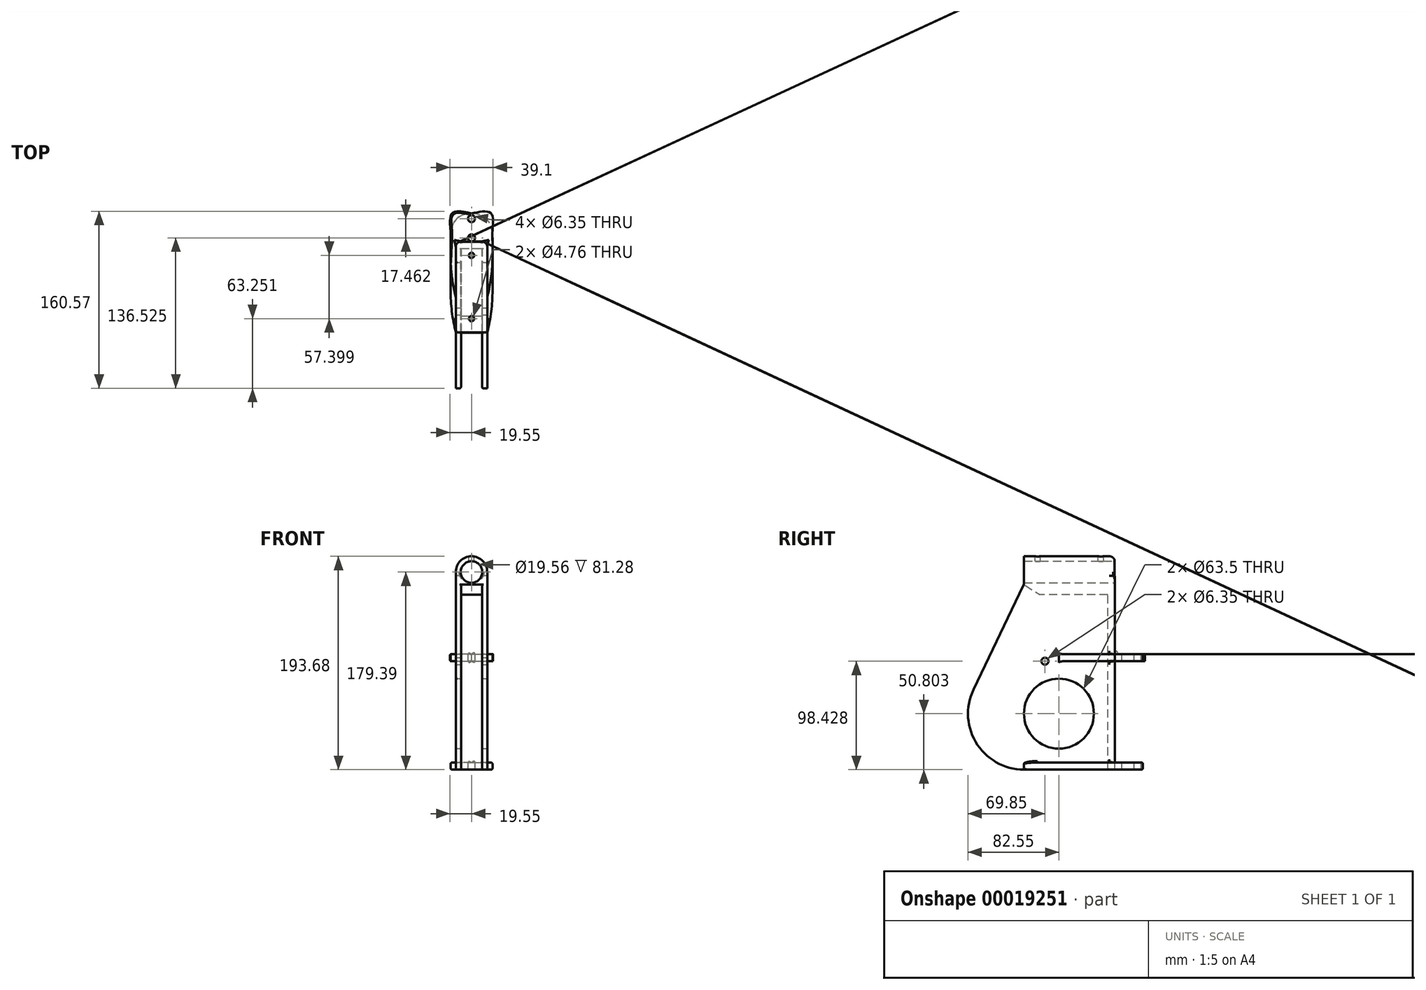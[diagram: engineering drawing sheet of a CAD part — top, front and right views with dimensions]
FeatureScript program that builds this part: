
annotation { "Feature Type Name" : "Feature", "Feature Type Description" : "" }
export const myFeature = defineFeature(function(context is Context, id is Id, definition is map)
    precondition{}
    {
        {
            var Q0;
            Q0=qCreatedBy(makeId("Front.planeOp"),FACE);
            var sketch = newSketch(context, id + "F0", { "sketchPlane" : qUnion([Q0])});
            skLineSegment(sketch, "E0.rect.top", {"start": v(-14.29, -96.84) * mm, "end": v(14.29, -96.84) * mm});
            skLineSegment(sketch, "E0.rect.left", {"start": v(-14.29, 82.55) * mm, "end": v(-14.29, -96.84) * mm});
            skLineSegment(sketch, "E0.rect.right", {"start": v(14.29, 82.55) * mm, "end": v(14.29, -96.84) * mm});
            skPoint(sketch, "E0.rect.middle", {"position": v(0, 0) * mm});
            skCircle(sketch, "E1", {"center": v(0, 82.55) * mm, "radius": 9.78 * mm});
            skArc(sketch, "E2", {"start": v(14.29, 82.55) * mm, "mid": v(0, 96.84) * mm, "end": v(-14.29, 82.55) * mm});
            skPoint(sketch, "E3.orphan", {"position": v(-14.29, 96.84) * mm});
            skPoint(sketch, "E4.orphan", {"position": v(14.29, 96.84) * mm});
            skSolve(sketch);
        }
        {
            var Q0;
            Q0=makeQuery(id+"F0.imprint","IMPRINT",FACE,{"disambiguationData":[TD([[makeQuery(id+"F0.imprint","IMPRINT",EDGE,{"derivedFrom":sQuery(id+"F0.wireOp",EDGE,"E0.rect.top")}),1.0]])]});
            extrude(context, id + "F1", {"entities" : qUnion([Q0]), "depth" : 133.35 * mm});
        }
        {
            var Q0;
            Q0=makeQuery(id+"F1.opExtrude","CAP_FACE",FACE,{"disambiguationData":[OSD([sQuery(id+"F0.wireOp",EDGE,"E0.rect.top"),sQuery(id+"F0.wireOp",EDGE,"E0.rect.left"),sQuery(id+"F0.wireOp",EDGE,"E0.rect.right"),sQuery(id+"F0.wireOp",EDGE,"E1"),sQuery(id+"F0.wireOp",EDGE,"E2")])],"isStart":false});
            var sketch = newSketch(context, id + "F2", { "sketchPlane" : qUnion([Q0])});
            skLineSegment(sketch, "E5.bottom", {"start": v(-9.53, -96.84) * mm, "end": v(9.52, -96.84) * mm});
            skLineSegment(sketch, "E5.top", {"start": v(-9.53, 61.91) * mm, "end": v(9.53, 61.91) * mm});
            skLineSegment(sketch, "E5.left", {"start": v(-9.53, -96.84) * mm, "end": v(-9.53, 61.91) * mm});
            skLineSegment(sketch, "E5.right", {"start": v(9.52, -96.84) * mm, "end": v(9.53, 61.91) * mm});
            skSolve(sketch);
        }
        {
            var Q0;
            Q0=makeQuery(id+"F2.imprint","IMPRINT",FACE,{"disambiguationData":[TD([[makeQuery(id+"F2.imprint","IMPRINT",EDGE,{"derivedFrom":sQuery(id+"F2.wireOp",EDGE,"E5.bottom")}),1.0]])]});
            extrude(context, id + "F3", {"entities" : qUnion([Q0]), "operationType" : NewBodyOperationType.REMOVE, "oppositeDirection" : true, "depth" : 127 * mm});
        }
        {
            var Q0;
            Q0=makeQuery(id+"F1.opExtrude","SWEPT_FACE",FACE,{"disambiguationData":[OSD([sQuery(id+"F0.wireOp",EDGE,"E0.rect.right")])]});
            var sketch = newSketch(context, id + "F4", { "sketchPlane" : qUnion([Q0])});
            skLineSegment(sketch, "E6", {"start": v(-82.55, 96.84) * mm, "end": v(-82.55, 71.44) * mm});
            skLineSegment(sketch, "E7", {"start": v(-82.55, 71.44) * mm, "end": v(-128.35, -24.07) * mm});
            skLineSegment(sketch, "E8", {"start": v(-82.55, -96.84) * mm, "end": v(0, -96.84) * mm});
            skLineSegment(sketch, "E9", {"start": v(0, -96.84) * mm, "end": v(0, 96.84) * mm});
            skLineSegment(sketch, "E10", {"start": v(0, 96.84) * mm, "end": v(-82.55, 96.84) * mm});
            skArc(sketch, "E11", {"start": v(-128.35, -24.07) * mm, "mid": v(-125.54, -73.1) * mm, "end": v(-82.55, -96.84) * mm});
            skLineSegment(sketch, "E12", {"start": v(-133.35, 96.84) * mm, "end": v(0, 96.84) * mm, "construction": true});
            skLineSegment(sketch, "E13", {"start": v(-82.55, 96.84) * mm, "end": v(-104.63, 136.99) * mm});
            skLineSegment(sketch, "E14", {"start": v(-104.63, 136.99) * mm, "end": v(-256.41, 126.94) * mm});
            skLineSegment(sketch, "E15", {"start": v(-256.41, 126.94) * mm, "end": v(-191.56, -96.27) * mm});
            skLineSegment(sketch, "E16", {"start": v(-191.56, -96.27) * mm, "end": v(-69.42, -120.07) * mm});
            skLineSegment(sketch, "E17", {"start": v(-69.42, -120.07) * mm, "end": v(-82.55, -96.84) * mm});
            skSolve(sketch);
        }
        {
            var Q0;
            {var subQ11=sQuery(id+"F4.wireOp",EDGE,"E13");Q0=makeQuery(id+"F4.imprint","IMPRINT",FACE,{"disambiguationData":[TD([[makeQuery(id+"F4.imprint","IMPRINT",EDGE,{"derivedFrom":subQ11}),1.0]])]});}
            var Q1;
            {var subQ8=sQuery(id+"F4.wireOp",EDGE,"E7");Q1=makeQuery(id+"F4.imprint","IMPRINT",FACE,{"disambiguationData":[TD([[makeQuery(id+"F4.imprint","IMPRINT",EDGE,{"derivedFrom":subQ8}),-1.0]])]});}
            var Q2;
            {var subQ0=sQuery(id+"F0.wireOp",EDGE,"E0.rect.right");var subQ1=makeQuery(id+"F1.opExtrude","CAP_EDGE",EDGE,{"disambiguationData":[OSD([subQ0])],"isStart":false});var subQ2=sQuery(id+"F4.wireOp",EDGE,"E11");var subQ3=makeQuery(id+"F4.imprint","INTERSECT",VERTEX,{"derivedFrom":[subQ1,subQ2]});Q2=makeQuery(id+"F4.imprint","IMPRINT",FACE,{"disambiguationData":[TD([[makeQuery(id+"F4.imprint","IMPRINT",EDGE,{"disambiguationData":[TD([[subQ3,-1.0]])],"derivedFrom":subQ1}),1.0]])]});}
            extrude(context, id + "F5", {"entities" : qUnion([Q0, Q1, Q2]), "operationType" : NewBodyOperationType.REMOVE, "endBound" : BoundingType.THROUGH_ALL, "oppositeDirection" : true, "depth" : 25.4 * mm});
        }
        {
            var Q0;
            Q0=makeQuery(id+"F5.boolean.opBoolean","INTERSECT",EDGE,{"derivedFrom":[makeQuery(id+"F3.boolean.opBoolean","COPY",FACE,{"derivedFrom":makeQuery(id+"F3.opExtrude","SWEPT_FACE",FACE,{"disambiguationData":[OSD([sQuery(id+"F2.wireOp",EDGE,"E5.top")])]})}),makeQuery(id+"F5.opExtrude","SWEPT_FACE",FACE,{"disambiguationData":[OSD([sQuery(id+"F4.wireOp",EDGE,"E7")])]})]});
            chamfer(context, id + "F6", {"entities" : qUnion([Q0]), "chamferType" : ChamferType.TWO_OFFSETS, "width1" : 19.05 * mm, "oppositeDirection" : false, "width2" : 10.16 * mm, "tangentPropagation" : true});
        }
        {
            var Q0;
            Q0=makeQuery(id+"F5.boolean.opBoolean","COPY",EDGE,{"derivedFrom":makeQuery(id+"F5.opExtrude","SWEPT_EDGE",EDGE,{"disambiguationData":[OSD([sQuery(id+"F4.wireOp",EDGE,"E6"),sQuery(id+"F4.wireOp",EDGE,"E7")])]})});
            fillet(context, id + "F7", {"entities" : qUnion([Q0]), "radius" : 6.35 * mm, "tangentPropagation" : true, "allowEdgeOverflow" : false});
        }
        {
            var Q0;
            Q0=makeQuery(id+"F1.opExtrude","SWEPT_FACE",FACE,{"disambiguationData":[OSD([sQuery(id+"F0.wireOp",EDGE,"E0.rect.right")])]});
            var sketch = newSketch(context, id + "F8", { "sketchPlane" : qUnion([Q0])});
            skCircle(sketch, "E18", {"center": v(-50.8, -46.04) * mm, "radius": 31.75 * mm});
            skSolve(sketch);
        }
        {
            var Q0;
            Q0=makeQuery(id+"F8.imprint","IMPRINT",FACE,{"disambiguationData":[TD([[makeQuery(id+"F8.imprint","IMPRINT",EDGE,{"derivedFrom":sQuery(id+"F8.wireOp",EDGE,"E18")}),1.0]])]});
            extrude(context, id + "F9", {"entities" : qUnion([Q0]), "operationType" : NewBodyOperationType.REMOVE, "endBound" : BoundingType.THROUGH_ALL, "oppositeDirection" : true, "depth" : 25.4 * mm});
        }
        {
            var Q0;
            Q0=makeQuery(id+"F1.opExtrude","SWEPT_FACE",FACE,{"disambiguationData":[OSD([sQuery(id+"F0.wireOp",EDGE,"E0.rect.top")])]});
            var sketch = newSketch(context, id + "F10", { "sketchPlane" : qUnion([Q0])});
            skLineSegment(sketch, "E19", {"start": v(0, -25.4) * mm, "end": v(0, 82.55) * mm, "construction": true});
            skLineSegment(sketch, "E20", {"start": v(-19.05, 44.45) * mm, "end": v(-19.05, 0) * mm});
            skArc(sketch, "E21", {"start": v(-14.29, 82.55) * mm, "mid": v(-17.85, 63.65) * mm, "end": v(-19.05, 44.45) * mm});
            skFitSpline(sketch, "E22", {"points": [v(0, -25.4) * mm, v(-19.05, 0) * mm], "startDerivative": vector(-53.17, 0) * mm, "endDerivative": vector(0, 31.35) * mm});
            skArc(sketch, "E23.MirrorCS", {"start": v(14.29, 82.55) * mm, "mid": v(17.85, 63.65) * mm, "end": v(19.05, 44.45) * mm});
            skLineSegment(sketch, "E24.MirrorCS", {"start": v(19.05, 44.45) * mm, "end": v(19.05, 0) * mm});
            skFitSpline(sketch, "E25.MirrorCS", {"points": [v(0, -25.4) * mm, v(19.05, 0) * mm], "startDerivative": vector(53.17, 0) * mm, "endDerivative": vector(0, 31.35) * mm});
            skLineSegment(sketch, "E26", {"start": v(-14.29, 82.55) * mm, "end": v(-9.53, 82.55) * mm});
            skLineSegment(sketch, "E27", {"start": v(-9.53, 82.55) * mm, "end": v(-9.53, 6.35) * mm});
            skLineSegment(sketch, "E28", {"start": v(-9.53, 6.35) * mm, "end": v(9.52, 6.35) * mm});
            skLineSegment(sketch, "E29", {"start": v(9.52, 6.35) * mm, "end": v(9.53, 82.55) * mm});
            skLineSegment(sketch, "E30", {"start": v(9.53, 82.55) * mm, "end": v(14.29, 82.55) * mm});
            skSolve(sketch);
        }
        {
            var Q0;
            Q0 = qSketchRegion(id + "F10", true);
            extrude(context, id + "F11", {"entities" : qUnion([Q0]), "operationType" : NewBodyOperationType.ADD, "oppositeDirection" : true, "depth" : 6.35 * mm});
        }
        {
            var Q0;
            Q0=makeQuery(id+"F11.boolean.opBoolean","MERGE",FACE,{"derivedFrom":[makeQuery(id+"F1.opExtrude","SWEPT_FACE",FACE,{"disambiguationData":[OSD([sQuery(id+"F0.wireOp",EDGE,"E0.rect.top")])]}),makeQuery(id+"F11.opExtrude","CAP_FACE",FACE,{"disambiguationData":[OSD([sQuery(id+"F10.wireOp",EDGE,"E20"),sQuery(id+"F10.wireOp",EDGE,"E21"),sQuery(id+"F10.wireOp",EDGE,"E22"),sQuery(id+"F10.wireOp",EDGE,"E23.MirrorCS"),sQuery(id+"F10.wireOp",EDGE,"E24.MirrorCS"),sQuery(id+"F10.wireOp",EDGE,"E25.MirrorCS"),sQuery(id+"F10.wireOp",EDGE,"E26"),sQuery(id+"F10.wireOp",EDGE,"E27"),sQuery(id+"F10.wireOp",EDGE,"E28"),sQuery(id+"F10.wireOp",EDGE,"E29"),sQuery(id+"F10.wireOp",EDGE,"E30")])],"isStart":true})]});
            cPlane(context, id + "F12", {"entities" : qUnion([Q0]), "cplaneType" : CPlaneType.OFFSET, "offset" : 101.6 * mm, "oppositeDirection" : true, "width" : 152.4 * mm, "height" : 152.4 * mm});
        }
        {
            var Q0;
            Q0=qCreatedBy(id+"F12.planeOp",FACE);
            var sketch = newSketch(context, id + "F13", { "sketchPlane" : qUnion([Q0])});
            skLineSegment(sketch, "E31.0", {"start": v(0, -25.4) * mm, "end": v(0, 82.55) * mm, "construction": true});
            skLineSegment(sketch, "E31.1", {"start": v(-19.05, 12.7) * mm, "end": v(-19.05, 0) * mm});
            skArc(sketch, "E31.2", {"start": v(-14.29, 50.8) * mm, "mid": v(-17.85, 31.9) * mm, "end": v(-19.05, 12.7) * mm});
            skFitSpline(sketch, "E31.3", {"points": [v(0, -25.4) * mm, v(-17.72, -25.4) * mm, v(-19.05, -10.45) * mm, v(-19.05, 0) * mm]});
            skArc(sketch, "E31.4", {"start": v(14.29, 50.8) * mm, "mid": v(17.85, 31.9) * mm, "end": v(19.05, 12.7) * mm});
            skLineSegment(sketch, "E31.5", {"start": v(19.05, 12.7) * mm, "end": v(19.05, 0) * mm});
            skFitSpline(sketch, "E31.6", {"points": [v(0, -25.4) * mm, v(17.72, -25.4) * mm, v(19.05, -10.45) * mm, v(19.05, 0) * mm]});
            skLineSegment(sketch, "E31.8", {"start": v(-9.53, 50.8) * mm, "end": v(-9.53, 6.35) * mm});
            skLineSegment(sketch, "E31.9", {"start": v(-9.53, 6.35) * mm, "end": v(9.52, 6.35) * mm});
            skLineSegment(sketch, "E31.10", {"start": v(9.53, 6.35) * mm, "end": v(9.53, 50.8) * mm});
            skLineSegment(sketch, "E32", {"start": v(-9.53, 50.8) * mm, "end": v(-14.29, 50.8) * mm});
            skLineSegment(sketch, "E33", {"start": v(9.53, 50.8) * mm, "end": v(14.29, 50.8) * mm});
            skSolve(sketch);
        }
        {
            var Q0;
            Q0=makeQuery(id+"F13.imprint","IMPRINT",FACE,{"disambiguationData":[TD([[makeQuery(id+"F13.imprint","IMPRINT",EDGE,{"derivedFrom":sQuery(id+"F13.wireOp",EDGE,"E31.1")}),1.0]])]});
            extrude(context, id + "F14", {"entities" : qUnion([Q0]), "operationType" : NewBodyOperationType.ADD, "endBound" : BoundingType.SYMMETRIC, "depth" : 6.35 * mm});
        }
        {
            var Q0;
            Q0=makeQuery(id+"F1.opExtrude","SWEPT_FACE",FACE,{"disambiguationData":[OSD([sQuery(id+"F0.wireOp",EDGE,"E0.rect.right")])]});
            var sketch = newSketch(context, id + "F15", { "sketchPlane" : qUnion([Q0])});
            skCircle(sketch, "E34", {"center": v(-63.5, 1.59) * mm, "radius": 3.18 * mm});
            skSolve(sketch);
        }
        {
            var Q0;
            Q0=makeQuery(id+"F15.imprint","IMPRINT",FACE,{"disambiguationData":[TD([[makeQuery(id+"F15.imprint","IMPRINT",EDGE,{"derivedFrom":sQuery(id+"F15.wireOp",EDGE,"E34")}),1.0]])]});
            extrude(context, id + "F16", {"entities" : qUnion([Q0]), "operationType" : NewBodyOperationType.REMOVE, "endBound" : BoundingType.THROUGH_ALL, "oppositeDirection" : true, "depth" : 25.4 * mm});
        }
        {
            var Q0;
            Q0=makeQuery(id+"F14.opExtrude","CAP_FACE",FACE,{"disambiguationData":[OSD([sQuery(id+"F13.wireOp",EDGE,"E31.1"),sQuery(id+"F13.wireOp",EDGE,"E31.2"),sQuery(id+"F13.wireOp",EDGE,"E31.3"),sQuery(id+"F13.wireOp",EDGE,"E31.4"),sQuery(id+"F13.wireOp",EDGE,"E31.5"),sQuery(id+"F13.wireOp",EDGE,"E31.6"),sQuery(id+"F13.wireOp",EDGE,"E31.8"),sQuery(id+"F13.wireOp",EDGE,"E31.9"),sQuery(id+"F13.wireOp",EDGE,"E31.10"),sQuery(id+"F13.wireOp",EDGE,"E32"),sQuery(id+"F13.wireOp",EDGE,"E33")])],"isStart":true});
            var sketch = newSketch(context, id + "F17", { "sketchPlane" : qUnion([Q0])});
            skCircle(sketch, "E35", {"center": v(0, 3.18) * mm, "radius": 3.18 * mm});
            skSolve(sketch);
        }
        {
            var Q0;
            Q0=makeQuery(id+"F17.imprint","IMPRINT",FACE,{"disambiguationData":[TD([[makeQuery(id+"F17.imprint","IMPRINT",EDGE,{"derivedFrom":sQuery(id+"F17.wireOp",EDGE,"E35")}),1.0]])]});
            extrude(context, id + "F18", {"entities" : qUnion([Q0]), "operationType" : NewBodyOperationType.REMOVE, "endBound" : BoundingType.THROUGH_ALL, "oppositeDirection" : true, "depth" : 25.4 * mm});
        }
        {
            var Q0;
            Q0=makeQuery(id+"F14.opExtrude","CAP_FACE",FACE,{"disambiguationData":[OSD([sQuery(id+"F13.wireOp",EDGE,"E31.1"),sQuery(id+"F13.wireOp",EDGE,"E31.2"),sQuery(id+"F13.wireOp",EDGE,"E31.3"),sQuery(id+"F13.wireOp",EDGE,"E31.4"),sQuery(id+"F13.wireOp",EDGE,"E31.5"),sQuery(id+"F13.wireOp",EDGE,"E31.6"),sQuery(id+"F13.wireOp",EDGE,"E31.8"),sQuery(id+"F13.wireOp",EDGE,"E31.9"),sQuery(id+"F13.wireOp",EDGE,"E31.10"),sQuery(id+"F13.wireOp",EDGE,"E32"),sQuery(id+"F13.wireOp",EDGE,"E33")])],"isStart":true});
            var sketch = newSketch(context, id + "F19", { "sketchPlane" : qUnion([Q0])});
            skCircle(sketch, "E36", {"center": v(0, 20.64) * mm, "radius": 3.18 * mm});
            skSolve(sketch);
        }
        {
            var Q0;
            Q0 = qSketchRegion(id + "F19", true);
            extrude(context, id + "F20", {"entities" : qUnion([Q0]), "operationType" : NewBodyOperationType.REMOVE, "endBound" : BoundingType.THROUGH_ALL, "oppositeDirection" : true, "depth" : 25.4 * mm});
        }
        {
            var Q0;
            {var subQ0=sQuery(id+"F0.wireOp",EDGE,"E0.rect.left");var subQ1=sQuery(id+"F0.wireOp",EDGE,"E0.rect.right");var subQ2=sQuery(id+"F0.wireOp",EDGE,"E1");var subQ3=sQuery(id+"F0.wireOp",EDGE,"E2");Q0=makeQuery(id+"F14.boolean.opBoolean","SPLIT",FACE,{"disambiguationData":[TD([makeQuery(id+"F1.opExtrude","SWEPT_FACE",FACE,{"disambiguationData":[OSD([subQ2])]})])],"derivedFrom":makeQuery(id+"F1.opExtrude","CAP_FACE",FACE,{"disambiguationData":[OSD([sQuery(id+"F0.wireOp",EDGE,"E0.rect.top"),subQ0,subQ1,subQ2,subQ3])],"isStart":true})});}
            var sketch = newSketch(context, id + "F21", { "sketchPlane" : qUnion([Q0])});
            skArc(sketch, "E37.0", {"start": v(-14.29, 82.55) * mm, "mid": v(0, 96.84) * mm, "end": v(14.29, 82.55) * mm});
            skPoint(sketch, "E38", {"position": v(0, 96.84) * mm});
            skSolve(sketch);
        }
        {
            var Q0;
            Q0=sQuery(id+"F21.wireOp",VERTEX,"E38");
            var Q1;
            Q1=makeQuery(id+"F14.opExtrude","CAP_FACE",FACE,{"disambiguationData":[OSD([sQuery(id+"F13.wireOp",EDGE,"E31.1"),sQuery(id+"F13.wireOp",EDGE,"E31.2"),sQuery(id+"F13.wireOp",EDGE,"E31.3"),sQuery(id+"F13.wireOp",EDGE,"E31.4"),sQuery(id+"F13.wireOp",EDGE,"E31.5"),sQuery(id+"F13.wireOp",EDGE,"E31.6"),sQuery(id+"F13.wireOp",EDGE,"E31.8"),sQuery(id+"F13.wireOp",EDGE,"E31.9"),sQuery(id+"F13.wireOp",EDGE,"E31.10"),sQuery(id+"F13.wireOp",EDGE,"E32"),sQuery(id+"F13.wireOp",EDGE,"E33")])],"isStart":true});
            cPlane(context, id + "F22", {"entities" : qUnion([Q0, Q1]), "cplaneType" : CPlaneType.PLANE_POINT, "offset" : 152.4 * mm, "width" : 152.4 * mm, "height" : 152.4 * mm});
        }
        {
            var Q0;
            Q0=qCreatedBy(id+"F22.planeOp",FACE);
            var sketch = newSketch(context, id + "F23", { "sketchPlane" : qUnion([Q0])});
            skLineSegment(sketch, "E39", {"start": v(0, 0) * mm, "end": v(0, -82.55) * mm, "construction": true});
            skCircle(sketch, "E40", {"center": v(0, -12.7) * mm, "radius": 2.38 * mm});
            skCircle(sketch, "E41", {"center": v(0, -70.1) * mm, "radius": 2.38 * mm});
            skSolve(sketch);
        }
        {
            var Q0;
            Q0=makeQuery(id+"F23.imprint","IMPRINT",FACE,{"disambiguationData":[TD([[makeQuery(id+"F23.imprint","IMPRINT",EDGE,{"derivedFrom":sQuery(id+"F23.wireOp",EDGE,"E40")}),1.0]])]});
            var Q1;
            Q1=makeQuery(id+"F23.imprint","IMPRINT",FACE,{"disambiguationData":[TD([[makeQuery(id+"F23.imprint","IMPRINT",EDGE,{"derivedFrom":sQuery(id+"F23.wireOp",EDGE,"E41")}),1.0]])]});
            extrude(context, id + "F24", {"entities" : qUnion([Q0, Q1]), "operationType" : NewBodyOperationType.REMOVE, "oppositeDirection" : true, "depth" : 6.35 * mm});
        }
        {
            var Q0;
            Q0=makeQuery(id+"F9.boolean.opBoolean","COPY",EDGE,{"derivedFrom":makeQuery(id+"F9.opExtrude","CAP_EDGE",EDGE,{"disambiguationData":[OSD([sQuery(id+"F8.wireOp",EDGE,"E18")])],"isStart":true})});
            var Q1;
            Q1=makeQuery(id+"F9.boolean.opBoolean","INTERSECT",EDGE,{"derivedFrom":[makeQuery(id+"F3.boolean.opBoolean","COPY",FACE,{"derivedFrom":makeQuery(id+"F3.opExtrude","SWEPT_FACE",FACE,{"disambiguationData":[OSD([sQuery(id+"F2.wireOp",EDGE,"E5.right")])]})}),makeQuery(id+"F9.opExtrude","SWEPT_FACE",FACE,{"disambiguationData":[OSD([sQuery(id+"F8.wireOp",EDGE,"E18")])]})]});
            var Q2;
            Q2=makeQuery(id+"F9.boolean.opBoolean","INTERSECT",EDGE,{"derivedFrom":[makeQuery(id+"F3.boolean.opBoolean","COPY",FACE,{"derivedFrom":makeQuery(id+"F3.opExtrude","SWEPT_FACE",FACE,{"disambiguationData":[OSD([sQuery(id+"F2.wireOp",EDGE,"E5.left")])]})}),makeQuery(id+"F9.opExtrude","SWEPT_FACE",FACE,{"disambiguationData":[OSD([sQuery(id+"F8.wireOp",EDGE,"E18")])]})]});
            var Q3;
            Q3=makeQuery(id+"F9.boolean.opBoolean","INTERSECT",EDGE,{"derivedFrom":[makeQuery(id+"F1.opExtrude","SWEPT_FACE",FACE,{"disambiguationData":[OSD([sQuery(id+"F0.wireOp",EDGE,"E0.rect.left")])]}),makeQuery(id+"F9.opExtrude","SWEPT_FACE",FACE,{"disambiguationData":[OSD([sQuery(id+"F8.wireOp",EDGE,"E18")])]})]});
            var Q4;
            Q4=makeQuery(id+"F5.boolean.opBoolean","COPY",EDGE,{"derivedFrom":makeQuery(id+"F5.opExtrude","CAP_EDGE",EDGE,{"disambiguationData":[OSD([sQuery(id+"F4.wireOp",EDGE,"E7")])],"isStart":true})});
            var Q5;
            Q5=makeQuery(id+"F14.boolean.opBoolean","INTERSECT",EDGE,{"derivedFrom":[makeQuery(id+"F1.opExtrude","SWEPT_FACE",FACE,{"disambiguationData":[OSD([sQuery(id+"F0.wireOp",EDGE,"E0.rect.right")])]}),makeQuery(id+"F14.opExtrude","CAP_FACE",FACE,{"disambiguationData":[OSD([sQuery(id+"F13.wireOp",EDGE,"E31.1"),sQuery(id+"F13.wireOp",EDGE,"E31.2"),sQuery(id+"F13.wireOp",EDGE,"E31.3"),sQuery(id+"F13.wireOp",EDGE,"E31.4"),sQuery(id+"F13.wireOp",EDGE,"E31.5"),sQuery(id+"F13.wireOp",EDGE,"E31.6"),sQuery(id+"F13.wireOp",EDGE,"E31.8"),sQuery(id+"F13.wireOp",EDGE,"E31.9"),sQuery(id+"F13.wireOp",EDGE,"E31.10"),sQuery(id+"F13.wireOp",EDGE,"E32"),sQuery(id+"F13.wireOp",EDGE,"E33")])],"isStart":true})]});
            var Q6;
            {var subQ0=sQuery(id+"F0.wireOp",EDGE,"E0.rect.right");var subQ1=makeQuery(id+"F1.opExtrude","CAP_FACE",FACE,{"disambiguationData":[OSD([sQuery(id+"F0.wireOp",EDGE,"E0.rect.top"),sQuery(id+"F0.wireOp",EDGE,"E0.rect.left"),subQ0,sQuery(id+"F0.wireOp",EDGE,"E1"),sQuery(id+"F0.wireOp",EDGE,"E2")])],"isStart":true});var subQ2=makeQuery(id+"F14.opExtrude","CAP_FACE",FACE,{"disambiguationData":[OSD([sQuery(id+"F13.wireOp",EDGE,"E31.1"),sQuery(id+"F13.wireOp",EDGE,"E31.2"),sQuery(id+"F13.wireOp",EDGE,"E31.3"),sQuery(id+"F13.wireOp",EDGE,"E31.4"),sQuery(id+"F13.wireOp",EDGE,"E31.5"),sQuery(id+"F13.wireOp",EDGE,"E31.6"),sQuery(id+"F13.wireOp",EDGE,"E31.8"),sQuery(id+"F13.wireOp",EDGE,"E31.9"),sQuery(id+"F13.wireOp",EDGE,"E31.10"),sQuery(id+"F13.wireOp",EDGE,"E32"),sQuery(id+"F13.wireOp",EDGE,"E33")])],"isStart":true});Q6=makeQuery(id+"F18.boolean.opBoolean","SPLIT",EDGE,{"disambiguationData":[TD([makeQuery(id+"F1.opExtrude","SWEPT_FACE",FACE,{"disambiguationData":[OSD([subQ0])]})])],"derivedFrom":makeQuery(id+"F14.boolean.opBoolean","INTERSECT",EDGE,{"derivedFrom":[subQ1,subQ2]})});}
            var Q7;
            {var subQ0=sQuery(id+"F0.wireOp",EDGE,"E0.rect.left");var subQ1=makeQuery(id+"F1.opExtrude","CAP_FACE",FACE,{"disambiguationData":[OSD([sQuery(id+"F0.wireOp",EDGE,"E0.rect.top"),subQ0,sQuery(id+"F0.wireOp",EDGE,"E0.rect.right"),sQuery(id+"F0.wireOp",EDGE,"E1"),sQuery(id+"F0.wireOp",EDGE,"E2")])],"isStart":true});var subQ2=makeQuery(id+"F14.opExtrude","CAP_FACE",FACE,{"disambiguationData":[OSD([sQuery(id+"F13.wireOp",EDGE,"E31.1"),sQuery(id+"F13.wireOp",EDGE,"E31.2"),sQuery(id+"F13.wireOp",EDGE,"E31.3"),sQuery(id+"F13.wireOp",EDGE,"E31.4"),sQuery(id+"F13.wireOp",EDGE,"E31.5"),sQuery(id+"F13.wireOp",EDGE,"E31.6"),sQuery(id+"F13.wireOp",EDGE,"E31.8"),sQuery(id+"F13.wireOp",EDGE,"E31.9"),sQuery(id+"F13.wireOp",EDGE,"E31.10"),sQuery(id+"F13.wireOp",EDGE,"E32"),sQuery(id+"F13.wireOp",EDGE,"E33")])],"isStart":true});Q7=makeQuery(id+"F18.boolean.opBoolean","SPLIT",EDGE,{"disambiguationData":[TD([makeQuery(id+"F1.opExtrude","SWEPT_FACE",FACE,{"disambiguationData":[OSD([subQ0])]})])],"derivedFrom":makeQuery(id+"F14.boolean.opBoolean","INTERSECT",EDGE,{"derivedFrom":[subQ1,subQ2]})});}
            var Q8;
            Q8=makeQuery(id+"F14.boolean.opBoolean","INTERSECT",EDGE,{"derivedFrom":[makeQuery(id+"F1.opExtrude","SWEPT_FACE",FACE,{"disambiguationData":[OSD([sQuery(id+"F0.wireOp",EDGE,"E0.rect.left")])]}),makeQuery(id+"F14.opExtrude","CAP_FACE",FACE,{"disambiguationData":[OSD([sQuery(id+"F13.wireOp",EDGE,"E31.1"),sQuery(id+"F13.wireOp",EDGE,"E31.2"),sQuery(id+"F13.wireOp",EDGE,"E31.3"),sQuery(id+"F13.wireOp",EDGE,"E31.4"),sQuery(id+"F13.wireOp",EDGE,"E31.5"),sQuery(id+"F13.wireOp",EDGE,"E31.6"),sQuery(id+"F13.wireOp",EDGE,"E31.8"),sQuery(id+"F13.wireOp",EDGE,"E31.9"),sQuery(id+"F13.wireOp",EDGE,"E31.10"),sQuery(id+"F13.wireOp",EDGE,"E32"),sQuery(id+"F13.wireOp",EDGE,"E33")])],"isStart":true})]});
            var Q9;
            Q9=makeQuery(id+"F14.boolean.opBoolean","INTERSECT",EDGE,{"derivedFrom":[makeQuery(id+"F1.opExtrude","SWEPT_FACE",FACE,{"disambiguationData":[OSD([sQuery(id+"F0.wireOp",EDGE,"E0.rect.left")])]}),makeQuery(id+"F14.opExtrude","CAP_FACE",FACE,{"disambiguationData":[OSD([sQuery(id+"F13.wireOp",EDGE,"E31.1"),sQuery(id+"F13.wireOp",EDGE,"E31.2"),sQuery(id+"F13.wireOp",EDGE,"E31.3"),sQuery(id+"F13.wireOp",EDGE,"E31.4"),sQuery(id+"F13.wireOp",EDGE,"E31.5"),sQuery(id+"F13.wireOp",EDGE,"E31.6"),sQuery(id+"F13.wireOp",EDGE,"E31.8"),sQuery(id+"F13.wireOp",EDGE,"E31.9"),sQuery(id+"F13.wireOp",EDGE,"E31.10"),sQuery(id+"F13.wireOp",EDGE,"E32"),sQuery(id+"F13.wireOp",EDGE,"E33")])],"isStart":false})]});
            var Q10;
            {var subQ0=sQuery(id+"F0.wireOp",EDGE,"E0.rect.left");var subQ1=makeQuery(id+"F1.opExtrude","CAP_FACE",FACE,{"disambiguationData":[OSD([sQuery(id+"F0.wireOp",EDGE,"E0.rect.top"),subQ0,sQuery(id+"F0.wireOp",EDGE,"E0.rect.right"),sQuery(id+"F0.wireOp",EDGE,"E1"),sQuery(id+"F0.wireOp",EDGE,"E2")])],"isStart":true});var subQ2=makeQuery(id+"F14.opExtrude","CAP_FACE",FACE,{"disambiguationData":[OSD([sQuery(id+"F13.wireOp",EDGE,"E31.1"),sQuery(id+"F13.wireOp",EDGE,"E31.2"),sQuery(id+"F13.wireOp",EDGE,"E31.3"),sQuery(id+"F13.wireOp",EDGE,"E31.4"),sQuery(id+"F13.wireOp",EDGE,"E31.5"),sQuery(id+"F13.wireOp",EDGE,"E31.6"),sQuery(id+"F13.wireOp",EDGE,"E31.8"),sQuery(id+"F13.wireOp",EDGE,"E31.9"),sQuery(id+"F13.wireOp",EDGE,"E31.10"),sQuery(id+"F13.wireOp",EDGE,"E32"),sQuery(id+"F13.wireOp",EDGE,"E33")])],"isStart":false});Q10=makeQuery(id+"F18.boolean.opBoolean","SPLIT",EDGE,{"disambiguationData":[TD([makeQuery(id+"F1.opExtrude","SWEPT_FACE",FACE,{"disambiguationData":[OSD([subQ0])]})])],"derivedFrom":makeQuery(id+"F14.boolean.opBoolean","INTERSECT",EDGE,{"derivedFrom":[subQ1,subQ2]})});}
            var Q11;
            {var subQ0=sQuery(id+"F0.wireOp",EDGE,"E0.rect.right");var subQ1=makeQuery(id+"F1.opExtrude","CAP_FACE",FACE,{"disambiguationData":[OSD([sQuery(id+"F0.wireOp",EDGE,"E0.rect.top"),sQuery(id+"F0.wireOp",EDGE,"E0.rect.left"),subQ0,sQuery(id+"F0.wireOp",EDGE,"E1"),sQuery(id+"F0.wireOp",EDGE,"E2")])],"isStart":true});var subQ2=makeQuery(id+"F14.opExtrude","CAP_FACE",FACE,{"disambiguationData":[OSD([sQuery(id+"F13.wireOp",EDGE,"E31.1"),sQuery(id+"F13.wireOp",EDGE,"E31.2"),sQuery(id+"F13.wireOp",EDGE,"E31.3"),sQuery(id+"F13.wireOp",EDGE,"E31.4"),sQuery(id+"F13.wireOp",EDGE,"E31.5"),sQuery(id+"F13.wireOp",EDGE,"E31.6"),sQuery(id+"F13.wireOp",EDGE,"E31.8"),sQuery(id+"F13.wireOp",EDGE,"E31.9"),sQuery(id+"F13.wireOp",EDGE,"E31.10"),sQuery(id+"F13.wireOp",EDGE,"E32"),sQuery(id+"F13.wireOp",EDGE,"E33")])],"isStart":false});Q11=makeQuery(id+"F18.boolean.opBoolean","SPLIT",EDGE,{"disambiguationData":[TD([makeQuery(id+"F1.opExtrude","SWEPT_FACE",FACE,{"disambiguationData":[OSD([subQ0])]})])],"derivedFrom":makeQuery(id+"F14.boolean.opBoolean","INTERSECT",EDGE,{"derivedFrom":[subQ1,subQ2]})});}
            var Q12;
            Q12=makeQuery(id+"F14.boolean.opBoolean","INTERSECT",EDGE,{"derivedFrom":[makeQuery(id+"F1.opExtrude","SWEPT_FACE",FACE,{"disambiguationData":[OSD([sQuery(id+"F0.wireOp",EDGE,"E0.rect.right")])]}),makeQuery(id+"F14.opExtrude","CAP_FACE",FACE,{"disambiguationData":[OSD([sQuery(id+"F13.wireOp",EDGE,"E31.1"),sQuery(id+"F13.wireOp",EDGE,"E31.2"),sQuery(id+"F13.wireOp",EDGE,"E31.3"),sQuery(id+"F13.wireOp",EDGE,"E31.4"),sQuery(id+"F13.wireOp",EDGE,"E31.5"),sQuery(id+"F13.wireOp",EDGE,"E31.6"),sQuery(id+"F13.wireOp",EDGE,"E31.8"),sQuery(id+"F13.wireOp",EDGE,"E31.9"),sQuery(id+"F13.wireOp",EDGE,"E31.10"),sQuery(id+"F13.wireOp",EDGE,"E32"),sQuery(id+"F13.wireOp",EDGE,"E33")])],"isStart":false})]});
            var Q13;
            Q13=makeQuery(id+"F11.boolean.opBoolean","INTERSECT",EDGE,{"derivedFrom":[makeQuery(id+"F1.opExtrude","SWEPT_FACE",FACE,{"disambiguationData":[OSD([sQuery(id+"F0.wireOp",EDGE,"E0.rect.right")])]}),makeQuery(id+"F11.opExtrude","CAP_FACE",FACE,{"disambiguationData":[OSD([sQuery(id+"F10.wireOp",EDGE,"E20"),sQuery(id+"F10.wireOp",EDGE,"E21"),sQuery(id+"F10.wireOp",EDGE,"E22"),sQuery(id+"F10.wireOp",EDGE,"E23.MirrorCS"),sQuery(id+"F10.wireOp",EDGE,"E24.MirrorCS"),sQuery(id+"F10.wireOp",EDGE,"E25.MirrorCS"),sQuery(id+"F10.wireOp",EDGE,"E26"),sQuery(id+"F10.wireOp",EDGE,"E27"),sQuery(id+"F10.wireOp",EDGE,"E28"),sQuery(id+"F10.wireOp",EDGE,"E29"),sQuery(id+"F10.wireOp",EDGE,"E30")])],"isStart":false})]});
            var Q14;
            {var subQ0=sQuery(id+"F0.wireOp",EDGE,"E0.rect.right");var subQ1=makeQuery(id+"F1.opExtrude","CAP_FACE",FACE,{"disambiguationData":[OSD([sQuery(id+"F0.wireOp",EDGE,"E0.rect.top"),sQuery(id+"F0.wireOp",EDGE,"E0.rect.left"),subQ0,sQuery(id+"F0.wireOp",EDGE,"E1"),sQuery(id+"F0.wireOp",EDGE,"E2")])],"isStart":true});var subQ2=makeQuery(id+"F11.opExtrude","CAP_FACE",FACE,{"disambiguationData":[OSD([sQuery(id+"F10.wireOp",EDGE,"E20"),sQuery(id+"F10.wireOp",EDGE,"E21"),sQuery(id+"F10.wireOp",EDGE,"E22"),sQuery(id+"F10.wireOp",EDGE,"E23.MirrorCS"),sQuery(id+"F10.wireOp",EDGE,"E24.MirrorCS"),sQuery(id+"F10.wireOp",EDGE,"E25.MirrorCS"),sQuery(id+"F10.wireOp",EDGE,"E26"),sQuery(id+"F10.wireOp",EDGE,"E27"),sQuery(id+"F10.wireOp",EDGE,"E28"),sQuery(id+"F10.wireOp",EDGE,"E29"),sQuery(id+"F10.wireOp",EDGE,"E30")])],"isStart":false});Q14=makeQuery(id+"F18.boolean.opBoolean","SPLIT",EDGE,{"disambiguationData":[TD([makeQuery(id+"F1.opExtrude","SWEPT_FACE",FACE,{"disambiguationData":[OSD([subQ0])]})])],"derivedFrom":makeQuery(id+"F11.boolean.opBoolean","INTERSECT",EDGE,{"derivedFrom":[subQ1,subQ2]})});}
            var Q15;
            {var subQ0=sQuery(id+"F0.wireOp",EDGE,"E0.rect.left");var subQ1=makeQuery(id+"F1.opExtrude","CAP_FACE",FACE,{"disambiguationData":[OSD([sQuery(id+"F0.wireOp",EDGE,"E0.rect.top"),subQ0,sQuery(id+"F0.wireOp",EDGE,"E0.rect.right"),sQuery(id+"F0.wireOp",EDGE,"E1"),sQuery(id+"F0.wireOp",EDGE,"E2")])],"isStart":true});var subQ2=makeQuery(id+"F11.opExtrude","CAP_FACE",FACE,{"disambiguationData":[OSD([sQuery(id+"F10.wireOp",EDGE,"E20"),sQuery(id+"F10.wireOp",EDGE,"E21"),sQuery(id+"F10.wireOp",EDGE,"E22"),sQuery(id+"F10.wireOp",EDGE,"E23.MirrorCS"),sQuery(id+"F10.wireOp",EDGE,"E24.MirrorCS"),sQuery(id+"F10.wireOp",EDGE,"E25.MirrorCS"),sQuery(id+"F10.wireOp",EDGE,"E26"),sQuery(id+"F10.wireOp",EDGE,"E27"),sQuery(id+"F10.wireOp",EDGE,"E28"),sQuery(id+"F10.wireOp",EDGE,"E29"),sQuery(id+"F10.wireOp",EDGE,"E30")])],"isStart":false});Q15=makeQuery(id+"F18.boolean.opBoolean","SPLIT",EDGE,{"disambiguationData":[TD([makeQuery(id+"F1.opExtrude","SWEPT_FACE",FACE,{"disambiguationData":[OSD([subQ0])]})])],"derivedFrom":makeQuery(id+"F11.boolean.opBoolean","INTERSECT",EDGE,{"derivedFrom":[subQ1,subQ2]})});}
            var Q16;
            Q16=makeQuery(id+"F11.boolean.opBoolean","INTERSECT",EDGE,{"derivedFrom":[makeQuery(id+"F1.opExtrude","SWEPT_FACE",FACE,{"disambiguationData":[OSD([sQuery(id+"F0.wireOp",EDGE,"E0.rect.left")])]}),makeQuery(id+"F11.opExtrude","CAP_FACE",FACE,{"disambiguationData":[OSD([sQuery(id+"F10.wireOp",EDGE,"E20"),sQuery(id+"F10.wireOp",EDGE,"E21"),sQuery(id+"F10.wireOp",EDGE,"E22"),sQuery(id+"F10.wireOp",EDGE,"E23.MirrorCS"),sQuery(id+"F10.wireOp",EDGE,"E24.MirrorCS"),sQuery(id+"F10.wireOp",EDGE,"E25.MirrorCS"),sQuery(id+"F10.wireOp",EDGE,"E26"),sQuery(id+"F10.wireOp",EDGE,"E27"),sQuery(id+"F10.wireOp",EDGE,"E28"),sQuery(id+"F10.wireOp",EDGE,"E29"),sQuery(id+"F10.wireOp",EDGE,"E30")])],"isStart":false})]});
            var Q17;
            Q17=makeQuery(id+"F11.opExtrude","CAP_EDGE",EDGE,{"disambiguationData":[OSD([sQuery(id+"F10.wireOp",EDGE,"E20")])],"isStart":false});
            var Q18;
            Q18=makeQuery(id+"F11.opExtrude","CAP_EDGE",EDGE,{"disambiguationData":[OSD([sQuery(id+"F10.wireOp",EDGE,"E21")])],"isStart":false});
            var Q19;
            Q19=makeQuery(id+"F11.opExtrude","CAP_EDGE",EDGE,{"disambiguationData":[OSD([sQuery(id+"F10.wireOp",EDGE,"E22")])],"isStart":false});
            var Q20;
            Q20=makeQuery(id+"F11.opExtrude","CAP_EDGE",EDGE,{"disambiguationData":[OSD([sQuery(id+"F10.wireOp",EDGE,"E25.MirrorCS")])],"isStart":false});
            var Q21;
            Q21=makeQuery(id+"F11.opExtrude","CAP_EDGE",EDGE,{"disambiguationData":[OSD([sQuery(id+"F10.wireOp",EDGE,"E24.MirrorCS")])],"isStart":false});
            var Q22;
            Q22=makeQuery(id+"F11.opExtrude","CAP_EDGE",EDGE,{"disambiguationData":[OSD([sQuery(id+"F10.wireOp",EDGE,"E23.MirrorCS")])],"isStart":false});
            var Q23;
            Q23=makeQuery(id+"F11.opExtrude","CAP_EDGE",EDGE,{"disambiguationData":[OSD([sQuery(id+"F10.wireOp",EDGE,"E21")])],"isStart":true});
            var Q24;
            Q24=makeQuery(id+"F14.opExtrude","CAP_EDGE",EDGE,{"disambiguationData":[OSD([sQuery(id+"F13.wireOp",EDGE,"E31.3")])],"isStart":false});
            var Q25;
            Q25=makeQuery(id+"F14.opExtrude","CAP_EDGE",EDGE,{"disambiguationData":[OSD([sQuery(id+"F13.wireOp",EDGE,"E31.3")])],"isStart":true});
            fillet(context, id + "F25", {"entities" : qUnion([Q0, Q1, Q2, Q3, Q4, Q5, Q6, Q7, Q8, Q9, Q10, Q11, Q12, Q13, Q14, Q15, Q16, Q17, Q18, Q19, Q20, Q21, Q22, Q23, Q24, Q25]), "radius" : 1.27 * mm, "tangentPropagation" : true, "allowEdgeOverflow" : false});
        }
        {
            var Q0;
            {var subQ0=sQuery(id+"F0.wireOp",EDGE,"E0.rect.right");Q0=makeQuery(id+"F14.boolean.opBoolean","SPLIT",EDGE,{"disambiguationData":[TD([makeQuery(id+"F11.opExtrude","CAP_FACE",FACE,{"disambiguationData":[OSD([sQuery(id+"F10.wireOp",EDGE,"E20"),sQuery(id+"F10.wireOp",EDGE,"E21"),sQuery(id+"F10.wireOp",EDGE,"E22"),sQuery(id+"F10.wireOp",EDGE,"E23.MirrorCS"),sQuery(id+"F10.wireOp",EDGE,"E24.MirrorCS"),sQuery(id+"F10.wireOp",EDGE,"E25.MirrorCS"),sQuery(id+"F10.wireOp",EDGE,"E26"),sQuery(id+"F10.wireOp",EDGE,"E27"),sQuery(id+"F10.wireOp",EDGE,"E28"),sQuery(id+"F10.wireOp",EDGE,"E29"),sQuery(id+"F10.wireOp",EDGE,"E30")])],"isStart":false})])],"derivedFrom":makeQuery(id+"F1.opExtrude","CAP_EDGE",EDGE,{"disambiguationData":[OSD([subQ0])],"isStart":true})});}
            var Q1;
            {var subQ0=sQuery(id+"F0.wireOp",EDGE,"E0.rect.right");var subQ1=sQuery(id+"F0.wireOp",EDGE,"E2");Q1=makeQuery(id+"F14.boolean.opBoolean","SPLIT",EDGE,{"disambiguationData":[TD([makeQuery(id+"F1.opExtrude","SWEPT_FACE",FACE,{"disambiguationData":[OSD([subQ1])]})])],"derivedFrom":makeQuery(id+"F1.opExtrude","CAP_EDGE",EDGE,{"disambiguationData":[OSD([subQ0])],"isStart":true})});}
            var Q2;
            {var subQ0=sQuery(id+"F0.wireOp",EDGE,"E0.rect.left");var subQ1=sQuery(id+"F0.wireOp",EDGE,"E2");Q2=makeQuery(id+"F14.boolean.opBoolean","SPLIT",EDGE,{"disambiguationData":[TD([makeQuery(id+"F1.opExtrude","SWEPT_FACE",FACE,{"disambiguationData":[OSD([subQ1])]})])],"derivedFrom":makeQuery(id+"F1.opExtrude","CAP_EDGE",EDGE,{"disambiguationData":[OSD([subQ0])],"isStart":true})});}
            var Q3;
            {var subQ0=sQuery(id+"F0.wireOp",EDGE,"E0.rect.left");Q3=makeQuery(id+"F14.boolean.opBoolean","SPLIT",EDGE,{"disambiguationData":[TD([makeQuery(id+"F11.opExtrude","CAP_FACE",FACE,{"disambiguationData":[OSD([sQuery(id+"F10.wireOp",EDGE,"E20"),sQuery(id+"F10.wireOp",EDGE,"E21"),sQuery(id+"F10.wireOp",EDGE,"E22"),sQuery(id+"F10.wireOp",EDGE,"E23.MirrorCS"),sQuery(id+"F10.wireOp",EDGE,"E24.MirrorCS"),sQuery(id+"F10.wireOp",EDGE,"E25.MirrorCS"),sQuery(id+"F10.wireOp",EDGE,"E26"),sQuery(id+"F10.wireOp",EDGE,"E27"),sQuery(id+"F10.wireOp",EDGE,"E28"),sQuery(id+"F10.wireOp",EDGE,"E29"),sQuery(id+"F10.wireOp",EDGE,"E30")])],"isStart":false})])],"derivedFrom":makeQuery(id+"F1.opExtrude","CAP_EDGE",EDGE,{"disambiguationData":[OSD([subQ0])],"isStart":true})});}
            fillet(context, id + "F26", {"entities" : qUnion([Q0, Q1, Q2, Q3]), "radius" : 5.08 * mm, "tangentPropagation" : true, "allowEdgeOverflow" : false});
        }
        {
            var Q0;
            Q0=makeQuery(id+"F5.boolean.opBoolean","INTERSECT",EDGE,{"derivedFrom":[makeQuery(id+"F3.boolean.opBoolean","COPY",FACE,{"derivedFrom":makeQuery(id+"F3.opExtrude","SWEPT_FACE",FACE,{"disambiguationData":[OSD([sQuery(id+"F2.wireOp",EDGE,"E5.left")])]})}),makeQuery(id+"F5.opExtrude","SWEPT_FACE",FACE,{"disambiguationData":[OSD([sQuery(id+"F4.wireOp",EDGE,"E7")])]})]});
            var Q1;
            Q1=makeQuery(id+"F5.boolean.opBoolean","INTERSECT",EDGE,{"derivedFrom":[makeQuery(id+"F3.boolean.opBoolean","COPY",FACE,{"derivedFrom":makeQuery(id+"F3.opExtrude","SWEPT_FACE",FACE,{"disambiguationData":[OSD([sQuery(id+"F2.wireOp",EDGE,"E5.right")])]})}),makeQuery(id+"F5.opExtrude","SWEPT_FACE",FACE,{"disambiguationData":[OSD([sQuery(id+"F4.wireOp",EDGE,"E7")])]})]});
            fillet(context, id + "F28", {"entities" : qUnion([Q0, Q1]), "radius" : 1.27 * mm, "tangentPropagation" : true, "allowEdgeOverflow" : false});
        }
        {
            var Q0;
            Q0=makeQuery(id+"F1.opExtrude","CAP_EDGE",EDGE,{"disambiguationData":[OSD([sQuery(id+"F0.wireOp",EDGE,"E1")])],"isStart":true});
            var Q1;
            {var subQ0=sQuery(id+"F0.wireOp",EDGE,"E0.rect.right");var subQ1=sQuery(id+"F0.wireOp",EDGE,"E2");var subQ2=sQuery(id+"F0.wireOp",EDGE,"E1");Q1=makeQuery(id+"F26.opFillet","BLEND_EDGE",EDGE,{"disambiguationData":[OD(0.0)],"blendedFrom":[makeQuery(id+"F14.boolean.opBoolean","SPLIT",EDGE,{"disambiguationData":[TD([makeQuery(id+"F1.opExtrude","SWEPT_FACE",FACE,{"disambiguationData":[OSD([subQ1])]})])],"derivedFrom":makeQuery(id+"F1.opExtrude","CAP_EDGE",EDGE,{"disambiguationData":[OSD([subQ0])],"isStart":true})}),makeQuery(id+"F1.opExtrude","SWEPT_FACE",FACE,{"disambiguationData":[OSD([subQ2])]})],"blendedInto":[makeQuery(id+"F1.opExtrude","SWEPT_FACE",FACE,{"disambiguationData":[OSD([subQ2])]})]});}
            var Q2;
            {var subQ0=sQuery(id+"F0.wireOp",EDGE,"E0.rect.right");var subQ1=sQuery(id+"F0.wireOp",EDGE,"E2");var subQ2=sQuery(id+"F0.wireOp",EDGE,"E1");Q2=makeQuery(id+"F26.opFillet","BLEND_EDGE",EDGE,{"disambiguationData":[OD(1.0)],"blendedFrom":[makeQuery(id+"F14.boolean.opBoolean","SPLIT",EDGE,{"disambiguationData":[TD([makeQuery(id+"F1.opExtrude","SWEPT_FACE",FACE,{"disambiguationData":[OSD([subQ1])]})])],"derivedFrom":makeQuery(id+"F1.opExtrude","CAP_EDGE",EDGE,{"disambiguationData":[OSD([subQ0])],"isStart":true})}),makeQuery(id+"F1.opExtrude","SWEPT_FACE",FACE,{"disambiguationData":[OSD([subQ2])]})],"blendedInto":[makeQuery(id+"F1.opExtrude","SWEPT_FACE",FACE,{"disambiguationData":[OSD([subQ2])]})]});}
            var Q3;
            {var subQ0=sQuery(id+"F0.wireOp",EDGE,"E0.rect.left");var subQ1=sQuery(id+"F0.wireOp",EDGE,"E2");var subQ2=sQuery(id+"F0.wireOp",EDGE,"E1");Q3=makeQuery(id+"F26.opFillet","BLEND_EDGE",EDGE,{"blendedFrom":[makeQuery(id+"F14.boolean.opBoolean","SPLIT",EDGE,{"disambiguationData":[TD([makeQuery(id+"F1.opExtrude","SWEPT_FACE",FACE,{"disambiguationData":[OSD([subQ1])]})])],"derivedFrom":makeQuery(id+"F1.opExtrude","CAP_EDGE",EDGE,{"disambiguationData":[OSD([subQ0])],"isStart":true})}),makeQuery(id+"F1.opExtrude","SWEPT_FACE",FACE,{"disambiguationData":[OSD([subQ2])]})],"blendedInto":[makeQuery(id+"F1.opExtrude","SWEPT_FACE",FACE,{"disambiguationData":[OSD([subQ2])]})]});}
            fillet(context, id + "F27", {"entities" : qUnion([Q0, Q1, Q2, Q3]), "radius" : 1.27 * mm, "tangentPropagation" : true, "allowEdgeOverflow" : false});
        }
    });
